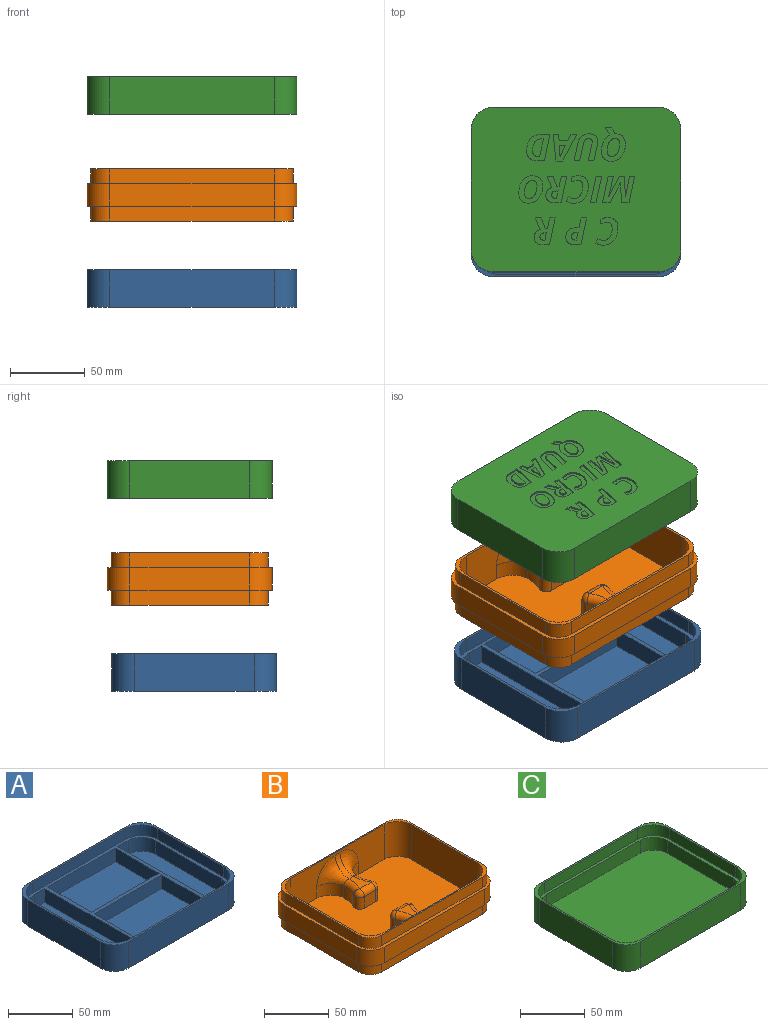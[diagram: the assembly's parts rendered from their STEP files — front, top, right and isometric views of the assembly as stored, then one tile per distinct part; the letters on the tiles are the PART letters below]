
ASSEMBLY  parts=3 mates=2
PART A: 43 faces, bbox 140x110x25 mm
  f0: plane 140x110mm, normal (0,0,1), area 810.7mm2, adj f2,f3,f4,f5,f6,f7,f8,f9
  f1: plane 140x110mm, normal (0,0,-1), area 15206.9mm2, adj f2,f3,f4,f5,f6,f7,f8,f9
  f2: plane 80x25mm, normal (1,0,0), area 2000mm2, adj f0,f1,f3,f9
  f3: cylinder r=15mm len=25mm, axis (0,0,-1), area 589mm2, adj f0,f1,f2,f4
  f4: plane 110x25mm, normal (0,1,0), area 2750mm2, adj f0,f1,f3,f5
  f5: cylinder r=15mm len=25mm, axis (0,0,-1), area 589mm2, adj f0,f1,f4,f6
  f6: plane 80x25mm, normal (-1,0,0), area 2000mm2, adj f0,f1,f5,f7
  f7: cylinder r=15mm len=25mm, axis (0,0,-1), area 589mm2, adj f0,f1,f6,f8
  f8: plane 110x25mm, normal (0,-1,0), area 2750mm2, adj f0,f1,f7,f9
  f9: cylinder r=15mm len=25mm, axis (0,0,-1), area 589mm2, adj f0,f1,f2,f8
  f10: plane 102x10mm, normal (0,1,0), area 1020mm2, adj f0,f11,f17,f35
  f11: cylinder r=17.5mm len=17.5mm, axis (0,0,1), area 274.9mm2, adj f0,f10,f12,f35
  f12: plane 72x10mm, normal (-1,0,0), area 720mm2, adj f0,f11,f13,f35
  f13: cylinder r=17.5mm len=17.5mm, axis (0,0,1), area 274.9mm2, adj f0,f12,f14,f35
  f14: plane 102x10mm, normal (0,-1,0), area 1020mm2, adj f0,f13,f15,f35
  f15: cylinder r=17.5mm len=17.5mm, axis (0,0,1), area 274.9mm2, adj f0,f14,f16,f35
  f16: plane 72x10mm, normal (1,0,0), area 720mm2, adj f0,f15,f17,f35
  f17: cylinder r=17.5mm len=17.5mm, axis (0,0,1), area 274.9mm2, adj f0,f10,f16,f35
  f18: plane 74x48mm, normal (0,0,1), area 3552mm2, adj f21,f22,f23,f24
  f19: plane 102x26mm, normal (0,0,1), area 2555.4mm2, adj f25,f26,f27,f28,f29,f30
  f20: plane 74x51mm, normal (0,0,1), area 3774mm2, adj f31,f32,f33,f34
  f21: plane 48x13mm, normal (1,0,0), area 624mm2, adj f18,f22,f23,f35
  f22: plane 74x13mm, normal (0,1,0), area 962mm2, adj f18,f21,f24,f35
  f23: plane 74x13mm, normal (0,-1,0), area 962mm2, adj f18,f21,f24,f35
  f24: plane 48x13mm, normal (-1,0,0), area 624mm2, adj f18,f22,f23,f35
  f25: plane 13x11mm, normal (0,1,0), area 143mm2, adj f19,f26,f30,f35
  f26: cylinder r=15mm len=15mm, axis (0,0,-1), area 306.3mm2, adj f19,f25,f27,f35
  f27: plane 72x13mm, normal (-1,0,0), area 936mm2, adj f19,f26,f28,f35
  f28: cylinder r=15mm len=15mm, axis (0,0,-1), area 306.3mm2, adj f19,f27,f29,f35
  f29: plane 13x11mm, normal (0,-1,0), area 143mm2, adj f19,f28,f30,f35
  f30: plane 102x13mm, normal (1,0,0), area 1326mm2, adj f19,f25,f29,f35
  f31: plane 51x13mm, normal (-1,0,0), area 663mm2, adj f20,f32,f33,f35
  f32: plane 74x13mm, normal (0,-1,0), area 962mm2, adj f20,f31,f34,f35
  f33: plane 74x13mm, normal (0,1,0), area 962mm2, adj f20,f31,f34,f35
  f34: plane 51x13mm, normal (1,0,0), area 663mm2, adj f20,f32,f33,f35
  f35: plane 137x107mm, normal (0,0,1), area 1959.3mm2, adj f10,f11,f12,f13,f14,f15,f16,f17
  f36: plane 102x13mm, normal (-1,0,0), area 1326mm2, adj f35,f37,f41,f42
  f37: plane 102x26mm, normal (0,0,1), area 2555.4mm2, adj f36,f38,f39,f40,f41,f42
  f38: cylinder r=15mm len=15mm, axis (0,0,-1), area 306.3mm2, adj f35,f37,f39,f42
  f39: plane 72x13mm, normal (1,0,0), area 936mm2, adj f35,f37,f38,f40
  f40: cylinder r=15mm len=15mm, axis (0,0,-1), area 306.3mm2, adj f35,f37,f39,f41
  f41: plane 13x11mm, normal (0,1,0), area 143mm2, adj f35,f36,f37,f40
  f42: plane 13x11mm, normal (0,-1,0), area 143mm2, adj f35,f36,f37,f38
PART B: 69 faces, bbox 140x110x35 mm
  f0: plane 135x105mm, normal (0,0,1), area 770mm2, adj f1,f2,f3,f4,f5,f6,f7,f8
  f1: plane 102x33mm, normal (0,1,0), area 2135.3mm2, adj f0,f2,f8,f9,f37,f38,f39,f40
  f2: cylinder r=15mm len=33mm, axis (0,0,-1), area 777.5mm2, adj f0,f1,f3,f9
  f3: plane 72x33mm, normal (1,0,0), area 2376mm2, adj f0,f2,f4,f9
  f4: cylinder r=15mm len=33mm, axis (0,0,-1), area 777.5mm2, adj f0,f3,f5,f9
  f5: plane 102x33mm, normal (0,-1,0), area 2135.3mm2, adj f0,f4,f6,f9,f32,f33,f34,f35
  f6: cylinder r=15mm len=33mm, axis (0,0,-1), area 777.5mm2, adj f0,f5,f7,f9
  f7: plane 72x33mm, normal (-1,0,0), area 2376mm2, adj f0,f6,f8,f9
  f8: cylinder r=15mm len=33mm, axis (0,0,-1), area 777.5mm2, adj f0,f1,f7,f9
  f9: plane 132x102mm, normal (0,0,1), area 11869.7mm2, adj f1,f2,f3,f4,f5,f6,f7,f8
  f10: plane 15.41x12.36mm, normal (0,0,1), area 114.5mm2, adj f22,f24,f26,f39
  f11: cylinder r=27.5mm len=14.31mm, axis (0,0,-1), area 162.3mm2, adj f9,f12,f26,f41
  f12: cylinder r=5mm len=11mm, axis (0,0,-1), area 111.8mm2, adj f9,f11,f13,f25
  f13: plane 12.36x11mm, normal (0,1,0), area 135.9mm2, adj f9,f12,f14,f24
  f14: cylinder r=5mm len=11mm, axis (0,0,-1), area 113.4mm2, adj f9,f13,f15,f23
  f15: cylinder r=26.72mm len=13.63mm, axis (0,0,-1), area 155.7mm2, adj f9,f14,f22,f37
  f16: plane 15.41x12.36mm, normal (0,0,1), area 114.5mm2, adj f27,f29,f31,f34
  f17: plane 12.36x11mm, normal (0,-1,0), area 135.9mm2, adj f9,f18,f21,f29
  f18: cylinder r=5mm len=11mm, axis (0,0,-1), area 113.4mm2, adj f9,f17,f19,f30
  f19: cylinder r=26.72mm len=13.63mm, axis (0,0,-1), area 155.7mm2, adj f9,f18,f31,f36
  f20: cylinder r=27.5mm len=14.31mm, axis (0,0,-1), area 162.3mm2, adj f9,f21,f27,f32
  f21: cylinder r=5mm len=11mm, axis (0,0,-1), area 111.8mm2, adj f9,f17,f20,f28
  f22: torus R=31.72mm, axis (0,0,1), area 115.9mm2, adj f10,f15,f23,f38
  f23: sphere r=5mm, area 51.6mm2, adj f14,f22,f24
  f24: cylinder r=5mm len=12.36mm, axis (1,0,0), area 97mm2, adj f10,f13,f23,f25
  f25: sphere r=5mm, area 50.8mm2, adj f12,f24,f26
  f26: torus R=32.5mm, axis (0,0,1), area 118.1mm2, adj f10,f11,f25,f40
  f27: torus R=32.5mm, axis (0,0,1), area 118.1mm2, adj f16,f20,f28,f33
  f28: sphere r=5mm, area 50.8mm2, adj f21,f27,f29
  f29: cylinder r=5mm len=12.36mm, axis (-1,0,0), area 97mm2, adj f16,f17,f28,f30
  f30: sphere r=5mm, area 51.6mm2, adj f18,f29,f31
  f31: torus R=31.72mm, axis (0,0,1), area 115.9mm2, adj f16,f19,f30,f35
  f32: cylinder r=15mm len=14.96mm, axis (0,0,-1), area 246.8mm2, adj f5,f9,f20,f33
  f33: bspline ~22.27x22.12mm, area 382.7mm2, adj f5,f27,f32,f34
  f34: cylinder r=15mm len=15mm, axis (1,0,0), area 122.9mm2, adj f5,f16,f33,f35
  f35: bspline ~22.26x21.98mm, area 384.6mm2, adj f5,f31,f34,f36
  f36: cylinder r=15mm len=14.99mm, axis (0,0,-1), area 252.9mm2, adj f5,f9,f19,f35
  f37: cylinder r=15mm len=14.99mm, axis (0,0,-1), area 252.9mm2, adj f1,f9,f15,f38
  f38: bspline ~22.26x21.98mm, area 384.6mm2, adj f1,f22,f37,f39
  f39: cylinder r=15mm len=15mm, axis (-1,0,0), area 122.9mm2, adj f1,f10,f38,f40
  f40: bspline ~22.27x22.12mm, area 382.7mm2, adj f1,f26,f39,f41
  f41: cylinder r=15mm len=14.96mm, axis (0,0,-1), area 246.8mm2, adj f1,f9,f11,f40
  f42: cylinder r=12.5mm len=12.5mm, axis (0,0,1), area 196.3mm2, adj f0,f43,f49,f50
  f43: plane 110x10mm, normal (0,-1,0), area 1100mm2, adj f0,f42,f44,f50
  f44: cylinder r=12.5mm len=12.5mm, axis (0,0,1), area 196.3mm2, adj f0,f43,f45,f50
  f45: plane 80x10mm, normal (-1,0,0), area 800mm2, adj f0,f44,f46,f50
  f46: cylinder r=12.5mm len=12.5mm, axis (0,0,1), area 196.3mm2, adj f0,f45,f47,f50
  f47: plane 110x10mm, normal (0,1,0), area 1100mm2, adj f0,f46,f48,f50
  f48: cylinder r=12.5mm len=12.5mm, axis (0,0,1), area 196.3mm2, adj f0,f47,f49,f50
  f49: plane 80x10mm, normal (1,0,0), area 800mm2, adj f0,f42,f48,f50
  f50: plane 140x110mm, normal (0,0,1), area 1166mm2, adj f42,f43,f44,f45,f46,f47,f48,f49
  f51: cylinder r=15mm len=15mm, axis (0,0,-1), area 353.4mm2, adj f50,f52,f58,f67
  f52: plane 110x15mm, normal (0,-1,0), area 1650mm2, adj f50,f51,f53,f67
  f53: cylinder r=15mm len=15mm, axis (0,0,-1), area 353.4mm2, adj f50,f52,f54,f67
  f54: plane 80x15mm, normal (-1,0,0), area 1200mm2, adj f50,f53,f55,f67
  f55: cylinder r=15mm len=15mm, axis (0,0,-1), area 353.4mm2, adj f50,f54,f56,f67
  f56: plane 110x15mm, normal (0,1,0), area 1650mm2, adj f50,f55,f57,f67
  f57: cylinder r=15mm len=15mm, axis (0,0,-1), area 353.4mm2, adj f50,f56,f58,f67
  f58: plane 80x15mm, normal (1,0,0), area 1200mm2, adj f50,f51,f57,f67
  f59: cylinder r=12.5mm len=12.5mm, axis (0,0,-1), area 196.3mm2, adj f60,f66,f67,f68
  f60: plane 110x10mm, normal (0,-1,0), area 1100mm2, adj f59,f61,f67,f68
  f61: cylinder r=12.5mm len=12.5mm, axis (0,0,-1), area 196.3mm2, adj f60,f62,f67,f68
  f62: plane 80x10mm, normal (1,0,0), area 800mm2, adj f61,f63,f67,f68
  f63: cylinder r=12.5mm len=12.5mm, axis (0,0,-1), area 196.3mm2, adj f62,f64,f67,f68
  f64: plane 110x10mm, normal (0,1,0), area 1100mm2, adj f63,f65,f67,f68
  f65: cylinder r=12.5mm len=12.5mm, axis (0,0,-1), area 196.3mm2, adj f64,f66,f67,f68
  f66: plane 80x10mm, normal (-1,0,0), area 800mm2, adj f59,f65,f67,f68
  f67: plane 140x110mm, normal (0,0,-1), area 1166mm2, adj f51,f52,f53,f54,f55,f56,f57,f58
  f68: plane 135x105mm, normal (0,0,-1), area 14040.9mm2, adj f59,f60,f61,f62,f63,f64,f65,f66
PART C: 246 faces, bbox 140x110x25 mm
  f0: plane 140x110mm, normal (0,0,-1), area 13247.1mm2, adj f2,f3,f4,f5,f6,f7,f8,f9
  f1: plane 140x110mm, normal (0,0,1), area 810.7mm2, adj f2,f3,f4,f5,f6,f7,f8,f9
  f2: plane 80x25mm, normal (1,0,0), area 2000mm2, adj f0,f1,f3,f9
  f3: cylinder r=15mm len=25mm, axis (0,0,-1), area 589mm2, adj f0,f1,f2,f4
  f4: plane 110x25mm, normal (0,1,0), area 2750mm2, adj f0,f1,f3,f5
  f5: cylinder r=15mm len=25mm, axis (0,0,-1), area 589mm2, adj f0,f1,f4,f6
  f6: plane 80x25mm, normal (-1,0,0), area 2000mm2, adj f0,f1,f5,f7
  f7: cylinder r=15mm len=25mm, axis (0,0,-1), area 589mm2, adj f0,f1,f6,f8
  f8: plane 110x25mm, normal (0,-1,0), area 2750mm2, adj f0,f1,f7,f9
  f9: cylinder r=15mm len=25mm, axis (0,0,-1), area 589mm2, adj f0,f1,f2,f8
  f10: plane 102x10mm, normal (0,1,0), area 1020mm2, adj f1,f11,f17,f18
  f11: cylinder r=17.5mm len=17.5mm, axis (0,0,1), area 274.9mm2, adj f1,f10,f12,f18
  f12: plane 72x10mm, normal (-1,0,0), area 720mm2, adj f1,f11,f13,f18
  f13: cylinder r=17.5mm len=17.5mm, axis (0,0,1), area 274.9mm2, adj f1,f12,f14,f18
  f14: plane 102x10mm, normal (0,-1,0), area 1020mm2, adj f1,f13,f15,f18
  f15: cylinder r=17.5mm len=17.5mm, axis (0,0,1), area 274.9mm2, adj f1,f14,f16,f18
  f16: plane 72x10mm, normal (1,0,0), area 720mm2, adj f1,f15,f17,f18
  f17: cylinder r=17.5mm len=17.5mm, axis (0,0,1), area 274.9mm2, adj f1,f10,f16,f18
  f18: plane 137x107mm, normal (0,0,1), area 1125.3mm2, adj f10,f11,f12,f13,f14,f15,f16,f17
  f19: plane 132x102mm, normal (0,0,1), area 13270.9mm2, adj f20,f21,f22,f23,f24,f25,f26,f27
  f20: plane 102x12mm, normal (0,1,0), area 1224mm2, adj f18,f19,f21,f27
  f21: cylinder r=15mm len=15mm, axis (0,0,-1), area 282.7mm2, adj f18,f19,f20,f22
  f22: plane 72x12mm, normal (-1,0,0), area 864mm2, adj f18,f19,f21,f23
  f23: cylinder r=15mm len=15mm, axis (0,0,-1), area 282.7mm2, adj f18,f19,f22,f24
  f24: plane 102x12mm, normal (0,-1,0), area 1224mm2, adj f18,f19,f23,f25
  f25: cylinder r=15mm len=15mm, axis (0,0,-1), area 282.7mm2, adj f18,f19,f24,f26
  f26: plane 72x12mm, normal (1,0,0), area 864mm2, adj f18,f19,f25,f27
  f27: cylinder r=15mm len=15mm, axis (0,0,-1), area 282.7mm2, adj f18,f19,f20,f26
  f28: extruded ~1.67x1mm, area 1.7mm2, adj f0,f29,f45,f46
  f29: extruded ~2.13x1mm, area 2.3mm2, adj f0,f28,f30,f46
  f30: plane 3.05x1.44mm, normal (-0.9,-0.43,0), area 3.4mm2, adj f0,f29,f31,f46
  f31: extruded ~2.54x1.01mm, area 2.7mm2, adj f0,f30,f32,f46
  f32: extruded ~2.71x1mm, area 2.7mm2, adj f0,f31,f33,f46
  f33: extruded ~4.88x1.4mm, area 5.2mm2, adj f0,f32,f34,f46
  f34: extruded ~4.09x3.39mm, area 5.4mm2, adj f0,f33,f35,f46
  f35: extruded ~5.89x1.27mm, area 6.1mm2, adj f0,f34,f36,f46
  f36: extruded ~5.17x1.72mm, area 5.6mm2, adj f0,f35,f37,f46
  f37: extruded ~4.82x1.83mm, area 5.3mm2, adj f0,f36,f38,f46
  f38: extruded ~4.88x1mm, area 5mm2, adj f0,f37,f39,f46
  f39: plane 3.18x1mm, normal (-1,0,0), area 3.2mm2, adj f0,f38,f40,f46
  f40: extruded ~4.13x1mm, area 4.3mm2, adj f0,f39,f41,f46
  f41: extruded ~2.67x1mm, area 2.9mm2, adj f0,f40,f42,f46
  f42: extruded ~3.03x1mm, area 3.2mm2, adj f0,f41,f43,f46
  f43: extruded ~4.13x1mm, area 4.2mm2, adj f0,f42,f44,f46
  f44: extruded ~2.91x2.07mm, area 3.6mm2, adj f0,f43,f45,f46
  f45: extruded ~2.9x1mm, area 3.1mm2, adj f0,f28,f44,f46
  f46: plane 18.38x14.8mm, normal (0,0,-1), area 109.2mm2, adj f28,f29,f30,f31,f32,f33,f34,f35
  f47: extruded ~5x1.8mm, area 5.5mm2, adj f0,f48,f62,f63
  f48: extruded ~5.1x1.75mm, area 5.5mm2, adj f0,f47,f49,f63
  f49: plane 4.84x1mm, normal (0,1,0), area 4.8mm2, adj f0,f48,f50,f63
  f50: plane 17.85x3.77mm, normal (0.98,0.21,0), area 18.2mm2, adj f0,f49,f51,f63
  f51: plane 5.5x1mm, normal (0,-1,0), area 5.5mm2, adj f0,f50,f52,f63
  f52: extruded ~5.34x1.32mm, area 5.6mm2, adj f0,f51,f53,f63
  f53: extruded ~3.84x3.46mm, area 5.2mm2, adj f0,f52,f62,f63
  f54: plane 1.29x1mm, normal (0,1,0), area 1.3mm2, adj f55,f61,f63,f64
  f55: plane 11.62x2.47mm, normal (-0.98,-0.21,0), area 11.9mm2, adj f54,f56,f63,f64
  f56: plane 1.4x1mm, normal (0,-1,0), area 1.4mm2, adj f55,f57,f63,f64
  f57: extruded ~2.55x1mm, area 2.8mm2, adj f56,f58,f63,f64
  f58: extruded ~2.86x1mm, area 3.1mm2, adj f57,f59,f63,f64
  f59: extruded ~4.12x1mm, area 4.2mm2, adj f58,f60,f63,f64
  f60: extruded ~2.73x2.1mm, area 3.5mm2, adj f59,f61,f63,f64
  f61: extruded ~3.15x1mm, area 3.3mm2, adj f54,f60,f63,f64
  f62: extruded ~5.94x1.2mm, area 6.1mm2, adj f0,f47,f53,f63
  f63: plane 17.85x15.5mm, normal (0,0,-1), area 155.1mm2, adj f47,f48,f49,f50,f51,f52,f53,f54
  f64: plane 11.62x7.3mm, normal (0,0,-1), area 59.3mm2, adj f54,f55,f56,f57,f58,f59,f60,f61
  f65: plane 4.25x1mm, normal (1,-0.07,0), area 4.3mm2, adj f0,f66,f78,f79
  f66: plane 3.63x1mm, normal (0,-1,0), area 3.6mm2, adj f0,f65,f67,f79
  f67: plane 17.92x1.79mm, normal (-1,0.1,0), area 18mm2, adj f0,f66,f68,f79
  f68: plane 4.55x1mm, normal (0,1,0), area 4.6mm2, adj f0,f67,f69,f79
  f69: plane 17.92x9.35mm, normal (0.89,0.46,0), area 20.2mm2, adj f0,f68,f70,f79
  f70: plane 3.91x1mm, normal (0,-1,0), area 3.9mm2, adj f0,f69,f71,f79
  f71: plane 4.25x2.1mm, normal (-0.9,-0.44,0), area 4.7mm2, adj f0,f70,f78,f79
  f72: plane 4.06x1mm, normal (0,1,0), area 4.1mm2, adj f73,f77,f79,f80
  f73: plane 4.7x2.29mm, normal (-0.9,-0.44,0), area 5.2mm2, adj f72,f74,f79,f80
  f74: extruded ~3.1x1.33mm, area 3.4mm2, adj f73,f75,f79,f80
  f75: plane 1x0.44mm, normal (1,0,0), area 0.4mm2, adj f74,f76,f79,f80
  f76: extruded ~3.09x1mm, area 3.1mm2, adj f75,f77,f79,f80
  f77: plane 4.27x1mm, normal (1,-0.07,0), area 4.3mm2, adj f72,f76,f79,f80
  f78: plane 5.77x1mm, normal (0,-1,0), area 5.8mm2, adj f0,f65,f71,f79
  f79: plane 17.92x15.7mm, normal (0,0,-1), area 136.9mm2, adj f65,f66,f67,f68,f69,f70,f71,f72
  f80: plane 7.8x4.06mm, normal (0,0,-1), area 14.9mm2, adj f72,f73,f74,f75,f76,f77
  f81: extruded ~4.92x1.71mm, area 5.3mm2, adj f0,f82,f103,f104
  f82: extruded ~4.82x1.76mm, area 5.3mm2, adj f0,f81,f83,f104
  f83: extruded ~4.91x1.45mm, area 5.2mm2, adj f0,f82,f84,f104
  f84: extruded ~4.17x3.33mm, area 5.4mm2, adj f0,f83,f85,f104
  f85: extruded ~5.95x1.21mm, area 6.1mm2, adj f0,f84,f86,f104
  f86: extruded ~5x1.75mm, area 5.4mm2, adj f0,f85,f87,f104
  f87: extruded ~4.88x1.8mm, area 5.3mm2, adj f0,f86,f88,f104
  f88: plane 1x0.32mm, normal (0,-1,0), area 0.3mm2, adj f0,f87,f89,f104
  f89: plane 4x2.17mm, normal (0.88,-0.48,0), area 4.6mm2, adj f0,f88,f90,f104
  f90: plane 4.38x1mm, normal (0,-1,0), area 4.4mm2, adj f0,f89,f91,f104
  f91: plane 4.8x3.1mm, normal (-0.84,0.54,0), area 5.7mm2, adj f0,f90,f92,f104
  f92: extruded ~4.12x4.08mm, area 5.9mm2, adj f0,f91,f103,f104
  f93: extruded ~2.23x1mm, area 2.5mm2, adj f94,f102,f104,f105
  f94: extruded ~2.68x1mm, area 2.9mm2, adj f93,f95,f104,f105
  f95: extruded ~4.36x1mm, area 4.4mm2, adj f94,f96,f104,f105
  f96: extruded ~3x1.9mm, area 3.6mm2, adj f95,f97,f104,f105
  f97: extruded ~2.69x1.06mm, area 3mm2, adj f96,f98,f104,f105
  f98: extruded ~2.29x1mm, area 2.5mm2, adj f97,f99,f104,f105
  f99: extruded ~2.71x1mm, area 2.9mm2, adj f98,f100,f104,f105
  f100: extruded ~4.24x1mm, area 4.3mm2, adj f99,f101,f104,f105
  f101: extruded ~3.07x1.94mm, area 3.7mm2, adj f100,f102,f104,f105
  f102: extruded ~2.71x1.12mm, area 3mm2, adj f93,f101,f104,f105
  f103: extruded ~6.78x1.5mm, area 7mm2, adj f0,f81,f92,f104
  f104: plane 22.38x15.98mm, normal (0,0,-1), area 174mm2, adj f81,f82,f83,f84,f85,f86,f87,f88
  f105: plane 12.05x8.38mm, normal (0,0,-1), area 78.6mm2, adj f93,f94,f95,f96,f97,f98,f99,f100
  f106: plane 3.73x1mm, normal (0,1,0), area 3.7mm2, adj f0,f107,f120,f121
  f107: plane 11.2x2.37mm, normal (0.98,0.21,0), area 11.4mm2, adj f0,f106,f108,f121
  f108: extruded ~2.79x1.27mm, area 3.1mm2, adj f0,f107,f109,f121
  f109: extruded ~2.38x1mm, area 2.6mm2, adj f0,f108,f110,f121
  f110: extruded ~2.3x2.17mm, area 3.6mm2, adj f0,f109,f111,f121
  f111: extruded ~1.53x1mm, area 1.5mm2, adj f0,f110,f112,f121
  f112: plane 11.22x2.37mm, normal (-0.98,-0.21,0), area 11.5mm2, adj f0,f111,f113,f121
  f113: plane 3.72x1mm, normal (0,1,0), area 3.7mm2, adj f0,f112,f114,f121
  f114: plane 11.27x2.39mm, normal (0.98,0.21,0), area 11.5mm2, adj f0,f113,f115,f121
  f115: extruded ~1.68x1mm, area 1.7mm2, adj f0,f114,f116,f121
  f116: extruded ~3.75x1.48mm, area 4.2mm2, adj f0,f115,f117,f121
  f117: extruded ~4.07x1.39mm, area 4.4mm2, adj f0,f116,f118,f121
  f118: extruded ~5.11x1.65mm, area 5.5mm2, adj f0,f117,f119,f121
  f119: extruded ~4.9x2.66mm, area 5.7mm2, adj f0,f118,f120,f121
  f120: plane 11.55x2.45mm, normal (-0.98,-0.21,0), area 11.8mm2, adj f0,f106,f119,f121
  f121: plane 18.09x15.78mm, normal (0,0,-1), area 140.4mm2, adj f106,f107,f108,f109,f110,f111,f112,f113
  f122: extruded ~1.67x1mm, area 1.7mm2, adj f0,f123,f139,f140
  f123: extruded ~2.13x1mm, area 2.3mm2, adj f0,f122,f124,f140
  f124: plane 3.05x1.44mm, normal (-0.9,-0.43,0), area 3.4mm2, adj f0,f123,f125,f140
  f125: extruded ~2.54x1.01mm, area 2.7mm2, adj f0,f124,f126,f140
  f126: extruded ~2.71x1mm, area 2.7mm2, adj f0,f125,f127,f140
  f127: extruded ~4.88x1.4mm, area 5.2mm2, adj f0,f126,f128,f140
  f128: extruded ~4.09x3.39mm, area 5.4mm2, adj f0,f127,f129,f140
  f129: extruded ~5.89x1.27mm, area 6.1mm2, adj f0,f128,f130,f140
  f130: extruded ~5.17x1.72mm, area 5.6mm2, adj f0,f129,f131,f140
  f131: extruded ~4.82x1.83mm, area 5.3mm2, adj f0,f130,f132,f140
  f132: extruded ~4.88x1mm, area 5mm2, adj f0,f131,f133,f140
  f133: plane 3.18x1mm, normal (-1,0,0), area 3.2mm2, adj f0,f132,f134,f140
  f134: extruded ~4.13x1mm, area 4.3mm2, adj f0,f133,f135,f140
  f135: extruded ~2.67x1mm, area 2.9mm2, adj f0,f134,f136,f140
  f136: extruded ~3.03x1mm, area 3.2mm2, adj f0,f135,f137,f140
  f137: extruded ~4.13x1mm, area 4.2mm2, adj f0,f136,f138,f140
  f138: extruded ~2.91x2.07mm, area 3.6mm2, adj f0,f137,f139,f140
  f139: extruded ~2.9x1mm, area 3.1mm2, adj f0,f122,f138,f140
  f140: plane 18.38x14.8mm, normal (0,0,-1), area 109.2mm2, adj f122,f123,f124,f125,f126,f127,f128,f129
  f141: plane 3.72x1mm, normal (0,-1,0), area 3.7mm2, adj f0,f142,f144,f145
  f142: plane 17.85x3.81mm, normal (-0.98,-0.21,0), area 18.2mm2, adj f0,f141,f143,f145
  f143: plane 3.72x1mm, normal (0,1,0), area 3.7mm2, adj f0,f142,f144,f145
  f144: plane 17.85x3.81mm, normal (0.98,0.21,0), area 18.2mm2, adj f0,f141,f143,f145
  f145: plane 17.85x7.53mm, normal (0,0,-1), area 66.4mm2, adj f141,f142,f143,f144
  f146: plane 1x0.05mm, normal (0,1,0), area 0.1mm2, adj f0,f147,f163,f164
  f147: plane 13.34x1mm, normal (-1,0.06,0), area 13.4mm2, adj f0,f146,f148,f164
  f148: plane 4.93x1mm, normal (0,1,0), area 4.9mm2, adj f0,f147,f149,f164
  f149: plane 17.85x3.77mm, normal (0.98,0.21,0), area 18.2mm2, adj f0,f148,f150,f164
  f150: plane 3.36x1mm, normal (0,-1,0), area 3.4mm2, adj f0,f149,f151,f164
  f151: extruded ~11.01x2.28mm, area 11.2mm2, adj f0,f150,f152,f164
  f152: extruded ~2.82x1mm, area 2.9mm2, adj f0,f151,f153,f164
  f153: plane 1x0.05mm, normal (0,-1,0), area 0.1mm2, adj f0,f152,f154,f164
  f154: plane 13.83x1mm, normal (1,-0.05,0), area 13.9mm2, adj f0,f153,f155,f164
  f155: plane 3.43x1mm, normal (0,-1,0), area 3.4mm2, adj f0,f154,f156,f164
  f156: plane 13.83x6.95mm, normal (-0.89,-0.45,0), area 15.5mm2, adj f0,f155,f157,f164
  f157: plane 1x0.06mm, normal (0,-1,0), area 0.1mm2, adj f0,f156,f158,f164
  f158: extruded ~5.38x1.28mm, area 5.5mm2, adj f0,f157,f159,f164
  f159: plane 8.45x1.77mm, normal (0.98,0.2,0), area 8.6mm2, adj f0,f158,f160,f164
  f160: plane 3.42x1mm, normal (0,-1,0), area 3.4mm2, adj f0,f159,f161,f164
  f161: plane 17.85x3.77mm, normal (-0.98,-0.21,0), area 18.2mm2, adj f0,f160,f162,f164
  f162: plane 5.16x1mm, normal (0,1,0), area 5.2mm2, adj f0,f161,f163,f164
  f163: plane 13.34x6.73mm, normal (0.89,0.45,0), area 14.9mm2, adj f0,f146,f162,f164
  f164: plane 21.47x17.85mm, normal (0,0,-1), area 213.8mm2, adj f146,f147,f148,f149,f150,f151,f152,f153
  f165: plane 5.3x1.13mm, normal (-0.98,-0.21,0), area 5.4mm2, adj f166,f179,f180,f243
  f166: plane 1x0.9mm, normal (0,-1,0), area 0.9mm2, adj f165,f167,f180,f243
  f167: extruded ~2.38x2.2mm, area 3.7mm2, adj f166,f168,f180,f243
  f168: extruded ~2.26x1mm, area 2.6mm2, adj f167,f169,f180,f243
  f169: extruded ~2.73x1mm, area 2.9mm2, adj f168,f179,f180,f243
  f170: extruded ~3.9x1.51mm, area 4.3mm2, adj f0,f171,f178,f180
  f171: extruded ~4.47x1.3mm, area 4.8mm2, adj f0,f170,f172,f180
  f172: plane 4.13x1mm, normal (0,1,0), area 4.1mm2, adj f0,f171,f173,f180
  f173: plane 17.85x3.77mm, normal (0.98,0.21,0), area 18.2mm2, adj f0,f172,f174,f180
  f174: plane 3.72x1mm, normal (0,-1,0), area 3.7mm2, adj f0,f173,f175,f180
  f175: plane 6.35x1.33mm, normal (-0.98,-0.2,0), area 6.5mm2, adj f0,f174,f176,f180
  f176: plane 1.05x1mm, normal (0,-1,0), area 1.1mm2, adj f0,f175,f177,f180
  f177: extruded ~5.71x1.68mm, area 6.1mm2, adj f0,f176,f178,f180
  f178: extruded ~4.62x2.07mm, area 5.3mm2, adj f0,f170,f177,f180
  f179: plane 1x0.68mm, normal (0,1,0), area 0.7mm2, adj f165,f169,f180,f243
  f180: plane 17.85x13.88mm, normal (0,0,-1), area 122.3mm2, adj f165,f166,f167,f168,f169,f170,f171,f172
  f181: plane 4.82x1.03mm, normal (-0.98,-0.21,0), area 4.9mm2, adj f182,f199,f200,f244
  f182: plane 1x0.9mm, normal (0,-1,0), area 0.9mm2, adj f181,f183,f200,f244
  f183: extruded ~1.83x1mm, area 1.9mm2, adj f182,f184,f200,f244
  f184: extruded ~1.5x1mm, area 1.7mm2, adj f183,f185,f200,f244
  f185: extruded ~2.13x1mm, area 2.4mm2, adj f184,f186,f200,f244
  f186: extruded ~2.49x1mm, area 2.6mm2, adj f185,f199,f200,f244
  f187: plane 1.45x1mm, normal (0,-1,0), area 1.5mm2, adj f0,f188,f198,f200
  f188: plane 6.85x2.52mm, normal (0.94,-0.35,0), area 7.3mm2, adj f0,f187,f189,f200
  f189: plane 4.05x1mm, normal (0,-1,0), area 4.1mm2, adj f0,f188,f190,f200
  f190: plane 7.58x3.19mm, normal (-0.92,0.39,0), area 8.2mm2, adj f0,f189,f191,f200
  f191: extruded ~2.92x2.06mm, area 3.6mm2, adj f0,f190,f192,f200
  f192: extruded ~3.31x1.01mm, area 3.5mm2, adj f0,f191,f193,f200
  f193: extruded ~3.65x1.45mm, area 4.1mm2, adj f0,f192,f194,f200
  f194: extruded ~4.35x1.25mm, area 4.6mm2, adj f0,f193,f195,f200
  f195: plane 4.38x1mm, normal (0,1,0), area 4.4mm2, adj f0,f194,f196,f200
  f196: plane 17.85x3.77mm, normal (0.98,0.21,0), area 18.2mm2, adj f0,f195,f197,f200
  f197: plane 3.72x1mm, normal (0,-1,0), area 3.7mm2, adj f0,f196,f198,f200
  f198: plane 6.85x1.45mm, normal (-0.98,-0.21,0), area 7mm2, adj f0,f187,f197,f200
  f199: plane 1x0.95mm, normal (0,1,0), area 1mm2, adj f181,f186,f200,f244
  f200: plane 17.85x13.95mm, normal (0,0,-1), area 147.8mm2, adj f181,f182,f183,f184,f185,f186,f187,f188
  f201: plane 4.82x1.03mm, normal (-0.98,-0.21,0), area 4.9mm2, adj f202,f219,f220,f245
  f202: plane 1x0.9mm, normal (0,-1,0), area 0.9mm2, adj f201,f203,f220,f245
  f203: extruded ~1.83x1mm, area 1.9mm2, adj f202,f204,f220,f245
  f204: extruded ~1.5x1mm, area 1.7mm2, adj f203,f205,f220,f245
  f205: extruded ~2.13x1mm, area 2.4mm2, adj f204,f206,f220,f245
  f206: extruded ~2.49x1mm, area 2.6mm2, adj f205,f219,f220,f245
  f207: plane 1.45x1mm, normal (0,-1,0), area 1.5mm2, adj f0,f208,f218,f220
  f208: plane 6.85x2.52mm, normal (0.94,-0.35,0), area 7.3mm2, adj f0,f207,f209,f220
  f209: plane 4.05x1mm, normal (0,-1,0), area 4.1mm2, adj f0,f208,f210,f220
  f210: plane 7.58x3.19mm, normal (-0.92,0.39,0), area 8.2mm2, adj f0,f209,f211,f220
  f211: extruded ~2.92x2.06mm, area 3.6mm2, adj f0,f210,f212,f220
  f212: extruded ~3.31x1.01mm, area 3.5mm2, adj f0,f211,f213,f220
  f213: extruded ~3.65x1.45mm, area 4.1mm2, adj f0,f212,f214,f220
  f214: extruded ~4.35x1.25mm, area 4.6mm2, adj f0,f213,f215,f220
  f215: plane 4.38x1mm, normal (0,1,0), area 4.4mm2, adj f0,f214,f216,f220
  f216: plane 17.85x3.77mm, normal (0.98,0.21,0), area 18.2mm2, adj f0,f215,f217,f220
  f217: plane 3.72x1mm, normal (0,-1,0), area 3.7mm2, adj f0,f216,f218,f220
  f218: plane 6.85x1.45mm, normal (-0.98,-0.21,0), area 7mm2, adj f0,f207,f217,f220
  f219: plane 1x0.95mm, normal (0,1,0), area 1mm2, adj f201,f206,f220,f245
  f220: plane 17.85x13.95mm, normal (0,0,-1), area 147.8mm2, adj f201,f202,f203,f204,f205,f206,f207,f208
  f221: extruded ~4.92x1.71mm, area 5.3mm2, adj f0,f222,f240,f241
  f222: extruded ~4.82x1.76mm, area 5.3mm2, adj f0,f221,f223,f241
  f223: extruded ~4.91x1.45mm, area 5.2mm2, adj f0,f222,f224,f241
  f224: extruded ~4.17x3.33mm, area 5.4mm2, adj f0,f223,f225,f241
  f225: extruded ~5.95x1.21mm, area 6.1mm2, adj f0,f224,f226,f241
  f226: extruded ~5x1.75mm, area 5.4mm2, adj f0,f225,f227,f241
  f227: extruded ~4.88x1.8mm, area 5.3mm2, adj f0,f226,f228,f241
  f228: extruded ~4.83x1.39mm, area 5.1mm2, adj f0,f227,f229,f241
  f229: extruded ~4.12x3.31mm, area 5.4mm2, adj f0,f228,f240,f241
  f230: extruded ~2.23x1mm, area 2.5mm2, adj f231,f239,f241,f242
  f231: extruded ~2.68x1mm, area 2.9mm2, adj f230,f232,f241,f242
  f232: extruded ~4.36x1mm, area 4.4mm2, adj f231,f233,f241,f242
  f233: extruded ~3x1.9mm, area 3.6mm2, adj f232,f234,f241,f242
  f234: extruded ~2.69x1.06mm, area 3mm2, adj f233,f235,f241,f242
  f235: extruded ~2.29x1mm, area 2.5mm2, adj f234,f236,f241,f242
  f236: extruded ~2.71x1mm, area 2.9mm2, adj f235,f237,f241,f242
  f237: extruded ~4.24x1mm, area 4.3mm2, adj f236,f238,f241,f242
  f238: extruded ~3.07x1.94mm, area 3.7mm2, adj f237,f239,f241,f242
  f239: extruded ~2.71x1.12mm, area 3mm2, adj f230,f238,f241,f242
  f240: extruded ~6.18x1.21mm, area 6.3mm2, adj f0,f221,f229,f241
  f241: plane 18.38x15.98mm, normal (0,0,-1), area 156.1mm2, adj f221,f222,f223,f224,f225,f226,f227,f228
  f242: plane 12.05x8.38mm, normal (0,0,-1), area 78.6mm2, adj f230,f231,f232,f233,f234,f235,f236,f237
  f243: plane 5.3x4.41mm, normal (0,0,-1), area 17.3mm2, adj f165,f166,f167,f168,f169,f179
  f244: plane 4.82x4.34mm, normal (0,0,-1), area 16mm2, adj f181,f182,f183,f184,f185,f186,f199
  f245: plane 4.82x4.34mm, normal (0,0,-1), area 16mm2, adj f201,f202,f203,f204,f205,f206,f219
PLACE A t=(62.75,-155.1,0)mm
PLACE B rot(axis=(0,-1,0),0deg) t=(62.75,-152.1,57.57)mm
PLACE C rot(axis=(0,1,0),180deg) t=(62.75,-152.1,154.01)mm
MATE slider B.f68 <-> A.f18  axis (0,0,-1) through (62.75,-152.1,57.57)mm
MATE slider B.f9 <-> C.f19  axis (0,0,1) through (62.75,-152.1,59.57)mm
